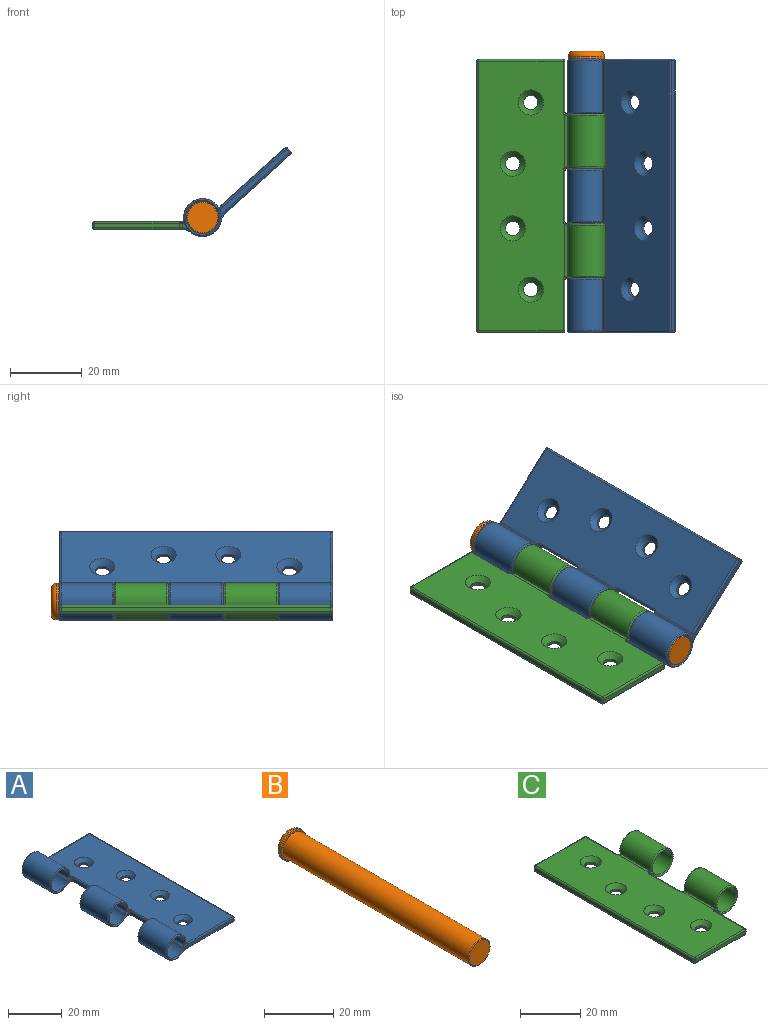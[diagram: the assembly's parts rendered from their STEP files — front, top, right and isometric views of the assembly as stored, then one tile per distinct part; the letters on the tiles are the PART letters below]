
ASSEMBLY  parts=3 mates=2
PART A: 94 faces, bbox 36.3x76x11.6 mm
  f0: cylinder r=5.25mm len=14.2mm, axis (0,1,0), area 412.4mm2, adj f2,f8,f69,f87
  f1: cylinder r=5.25mm len=14.2mm, axis (0,1,0), area 412.4mm2, adj f3,f9,f46,f78
  f2: plane 15.21x0.8mm, normal (0,0,-1), area 11.4mm2, adj f0,f4,f69,f71,f87,f90
  f3: plane 15.21x0.8mm, normal (0,0,-1), area 11.4mm2, adj f1,f5,f45,f46,f78,f80
  f4: cylinder r=4.5mm len=14.2mm, axis (0,1,0), area 382.9mm2, adj f2,f6,f71,f90
  f5: cylinder r=4.5mm len=14.2mm, axis (0,1,0), area 382.9mm2, adj f3,f7,f45,f80
  f6: cylinder r=2.39mm len=14.47mm, axis (0,1,0), area 36mm2, adj f4,f14,f73,f75,f92,f93
  f7: cylinder r=2.39mm len=14.33mm, axis (0,1,0), area 35.9mm2, adj f5,f14,f43,f82,f84
  f8: cylinder r=4.96mm len=14.47mm, axis (0,1,0), area 44.3mm2, adj f0,f16,f66,f68,f85,f88
  f9: cylinder r=4.96mm len=14.33mm, axis (0,1,0), area 44.3mm2, adj f1,f16,f48,f76,f77
  f10: cylinder r=5.25mm len=14.2mm, axis (0,1,0), area 412.4mm2, adj f11,f17,f51,f60
  f11: plane 15.21x0.8mm, normal (0,0,-1), area 11.4mm2, adj f10,f12,f51,f52,f60,f63
  f12: cylinder r=4.5mm len=14.2mm, axis (0,1,0), area 382.9mm2, adj f11,f13,f52,f63
  f13: cylinder r=2.39mm len=14.33mm, axis (0,1,0), area 35.9mm2, adj f12,f14,f49,f65,f67
  f14: plane 75x24mm, normal (0,0,1), area 1630.6mm2, adj f6,f7,f13,f21,f23,f25,f27,f41
  f15: plane 75x1.3mm, normal (1,0,0), area 97.5mm2, adj f38,f39,f42,f55
  f16: plane 75x24mm, normal (0,0,-1), area 1734.3mm2, adj f8,f9,f17,f20,f22,f24,f26,f50
  f17: cylinder r=4.96mm len=14.33mm, axis (0,1,0), area 44.3mm2, adj f10,f16,f54,f58,f61
  f18: plane 26.22x1.77mm, normal (0,-1,0), area 33.2mm2, adj f39,f47,f49,f52,f54,f56
  f19: plane 26.22x1.77mm, normal (0,1,0), area 33.2mm2, adj f38,f41,f43,f45,f48,f50
  f20: cylinder r=2mm len=4mm, axis (0,0,1), area 10.1mm2, adj f16,f21
  f21: cone r=2mm half-angle=45deg, axis (0,0,1), area 36.7mm2, adj f14,f20
  f22: cylinder r=2mm len=4mm, axis (0,0,1), area 10.1mm2, adj f16,f23
  f23: cone r=2mm half-angle=45deg, axis (0,0,1), area 36.7mm2, adj f14,f22
  f24: cylinder r=2mm len=4mm, axis (0,0,1), area 10.1mm2, adj f16,f25
  f25: cone r=2mm half-angle=45deg, axis (0,0,1), area 36.7mm2, adj f14,f24
  f26: cylinder r=2mm len=4mm, axis (0,0,1), area 10.1mm2, adj f16,f27
  f27: cone r=2mm half-angle=45deg, axis (0,0,1), area 36.7mm2, adj f14,f26
  f28: plane 14.2x1.3mm, normal (-1,0,0), area 18.5mm2, adj f34,f35,f81,f89
  f29: plane 1.72x1.7mm, normal (0,-1,0), area 1.3mm2, adj f34,f77,f80,f82
  f30: plane 1.72x1.7mm, normal (0,1,0), area 1.3mm2, adj f35,f88,f90,f92
  f31: plane 14.2x1.3mm, normal (-1,0,0), area 18.5mm2, adj f36,f37,f62,f72
  f32: plane 1.72x1.7mm, normal (0,1,0), area 1.3mm2, adj f36,f61,f63,f65
  f33: plane 1.72x1.7mm, normal (0,-1,0), area 1.3mm2, adj f37,f68,f71,f73
  f34: cylinder r=0.5mm len=1.32mm, axis (0,0,-1), area 1mm2, adj f28,f29,f76,f79,f84,f86
  f35: cylinder r=0.5mm len=1.32mm, axis (0,0,1), area 1mm2, adj f28,f30,f83,f85,f91,f93
  f36: cylinder r=0.5mm len=1.32mm, axis (0,0,-1), area 1mm2, adj f31,f32,f58,f59,f67,f70
  f37: cylinder r=0.5mm len=1.32mm, axis (0,0,1), area 1mm2, adj f31,f33,f64,f66,f74,f75
  f38: cylinder r=0.5mm len=1.3mm, axis (0,0,-1), area 1mm2, adj f15,f19,f40,f53
  f39: cylinder r=0.5mm len=1.3mm, axis (0,0,1), area 1mm2, adj f15,f18,f44,f57
  f40: sphere r=0.5mm, area 0.4mm2, adj f38,f41,f42
  f41: cylinder r=0.5mm len=24mm, axis (1,0,0), area 18.8mm2, adj f14,f19,f40,f43
  f42: cylinder r=0.5mm len=75mm, axis (0,1,0), area 58.9mm2, adj f14,f15,f40,f44
  f43: torus R=1.89mm, axis (0,-1,0), area 1.8mm2, adj f7,f19,f41,f45
  f44: sphere r=0.5mm, area 0.4mm2, adj f39,f42,f47
  f45: torus R=5mm, axis (0,-1,0), area 18.5mm2, adj f3,f5,f19,f43,f46,f48
  f46: torus R=4.75mm, axis (0,-1,0), area 18.7mm2, adj f1,f3,f45,f48
  f47: cylinder r=0.5mm len=24mm, axis (-1,0,0), area 18.8mm2, adj f14,f18,f44,f49
  f48: torus R=5.46mm, axis (0,-1,0), area 2.5mm2, adj f9,f19,f45,f46,f50
  f49: torus R=1.89mm, axis (0,-1,0), area 1.8mm2, adj f13,f18,f47,f52
  f50: cylinder r=0.5mm len=24mm, axis (-1,0,0), area 18.8mm2, adj f16,f19,f48,f53
  f51: torus R=4.75mm, axis (0,-1,0), area 18.7mm2, adj f10,f11,f52,f54
  f52: torus R=5mm, axis (0,-1,0), area 18.5mm2, adj f11,f12,f18,f49,f51,f54
  f53: sphere r=0.5mm, area 0.4mm2, adj f38,f50,f55
  f54: torus R=5.46mm, axis (0,-1,0), area 2.5mm2, adj f17,f18,f51,f52,f56
  f55: cylinder r=0.5mm len=75mm, axis (0,1,0), area 58.9mm2, adj f15,f16,f53,f57
  f56: cylinder r=0.5mm len=24mm, axis (1,0,0), area 18.8mm2, adj f16,f18,f54,f57
  f57: sphere r=0.5mm, area 0.4mm2, adj f39,f55,f56
  f58: bspline ~0.72x0.61mm, area 0.3mm2, adj f17,f36,f59,f61
  f59: torus R=1mm, axis (0,0,1), area 0.6mm2, adj f16,f36,f58,f62
  f60: torus R=4.75mm, axis (0,-1,0), area 18.7mm2, adj f10,f11,f61,f63
  f61: torus R=5.46mm, axis (0,-1,0), area 2.1mm2, adj f17,f32,f58,f60,f63
  f62: cylinder r=0.5mm len=14.2mm, axis (0,-1,0), area 11.2mm2, adj f16,f31,f59,f64
  f63: torus R=5mm, axis (0,-1,0), area 18.5mm2, adj f11,f12,f32,f60,f61,f65
  f64: torus R=1mm, axis (0,0,1), area 0.6mm2, adj f16,f37,f62,f66
  f65: torus R=1.89mm, axis (0,-1,0), area 1.4mm2, adj f13,f32,f63,f67
  f66: bspline ~0.72x0.61mm, area 0.3mm2, adj f8,f37,f64,f68
  f67: bspline ~0.83x0.6mm, area 0.3mm2, adj f13,f36,f65,f70
  f68: torus R=5.46mm, axis (0,-1,0), area 2.1mm2, adj f8,f33,f66,f69,f71
  f69: torus R=4.75mm, axis (0,-1,0), area 18.7mm2, adj f0,f2,f68,f71
  f70: torus R=1mm, axis (0,0,-1), area 0.6mm2, adj f14,f36,f67,f72
  f71: torus R=5mm, axis (0,-1,0), area 18.5mm2, adj f2,f4,f33,f68,f69,f73
  f72: cylinder r=0.5mm len=14.2mm, axis (0,-1,0), area 11.2mm2, adj f14,f31,f70,f74
  f73: torus R=1.89mm, axis (0,-1,0), area 1.4mm2, adj f6,f33,f71,f75
  f74: torus R=1mm, axis (0,0,-1), area 0.6mm2, adj f14,f37,f72,f75
  f75: bspline ~0.83x0.6mm, area 0.3mm2, adj f6,f37,f73,f74
  f76: bspline ~0.72x0.61mm, area 0.3mm2, adj f9,f34,f77,f79
  f77: torus R=5.46mm, axis (0,-1,0), area 2.1mm2, adj f9,f29,f76,f78,f80
  f78: torus R=4.75mm, axis (0,-1,0), area 18.7mm2, adj f1,f3,f77,f80
  f79: torus R=1mm, axis (0,0,1), area 0.6mm2, adj f16,f34,f76,f81
  f80: torus R=5mm, axis (0,-1,0), area 18.5mm2, adj f3,f5,f29,f77,f78,f82
  f81: cylinder r=0.5mm len=14.2mm, axis (0,1,0), area 11.2mm2, adj f16,f28,f79,f83
  f82: torus R=1.89mm, axis (0,-1,0), area 1.4mm2, adj f7,f29,f80,f84
  f83: torus R=1mm, axis (0,0,1), area 0.6mm2, adj f16,f35,f81,f85
  f84: bspline ~0.83x0.6mm, area 0.3mm2, adj f7,f34,f82,f86
  f85: bspline ~0.72x0.61mm, area 0.3mm2, adj f8,f35,f83,f88
  f86: torus R=1mm, axis (0,0,-1), area 0.6mm2, adj f14,f34,f84,f89
  f87: torus R=4.75mm, axis (0,-1,0), area 18.7mm2, adj f0,f2,f88,f90
  f88: torus R=5.46mm, axis (0,-1,0), area 2.1mm2, adj f8,f30,f85,f87,f90
  f89: cylinder r=0.5mm len=14.2mm, axis (0,-1,0), area 11.2mm2, adj f14,f28,f86,f91
  f90: torus R=5mm, axis (0,-1,0), area 18.5mm2, adj f2,f4,f30,f87,f88,f92
  f91: torus R=1mm, axis (0,0,-1), area 0.6mm2, adj f14,f35,f89,f93
  f92: torus R=1.89mm, axis (0,-1,0), area 1.4mm2, adj f6,f30,f90,f93
  f93: bspline ~0.83x0.6mm, area 0.3mm2, adj f6,f35,f91,f92
PART B: 8 faces, bbox 11x78.2x11 mm
  f0: cylinder r=4.4mm len=75.8mm, axis (0,1,0), area 2095.6mm2, adj f2,f5
  f1: plane 8.4x8.4mm, normal (0,-1,0), area 55.4mm2, adj f2
  f2: torus R=4.2mm, axis (0,-1,0), area 8.5mm2, adj f0,f1
  f3: cylinder r=5.1mm len=10.21mm, axis (0,-1,0), area 16mm2, adj f6,f7
  f4: plane 7.21x7.21mm, normal (0,1,0), area 40.8mm2, adj f6
  f5: plane 9.81x9.81mm, normal (0,-1,0), area 14.7mm2, adj f0,f7
  f6: torus R=3.6mm, axis (0,1,0), area 67.5mm2, adj f3,f4
  f7: torus R=4.9mm, axis (0,1,0), area 9.9mm2, adj f3,f5
PART C: 90 faces, bbox 36.3x76x11.6 mm
  f0: cylinder r=5.25mm len=14.2mm, axis (0,1,0), area 412.4mm2, adj f2,f8,f59,f83
  f1: cylinder r=5.25mm len=14.2mm, axis (0,1,0), area 412.4mm2, adj f3,f9,f46,f74
  f2: plane 15.21x0.8mm, normal (0,0,-1), area 11.4mm2, adj f0,f4,f59,f61,f83,f86
  f3: plane 15.21x0.8mm, normal (0,0,-1), area 11.4mm2, adj f1,f5,f46,f49,f74,f76
  f4: cylinder r=4.5mm len=14.2mm, axis (0,1,0), area 382.9mm2, adj f2,f6,f61,f86
  f5: cylinder r=4.5mm len=14.2mm, axis (0,1,0), area 382.9mm2, adj f3,f7,f49,f76
  f6: cylinder r=2.39mm len=14.47mm, axis (0,1,0), area 36mm2, adj f4,f10,f63,f65,f88,f89
  f7: cylinder r=2.39mm len=14.47mm, axis (0,1,0), area 36mm2, adj f5,f10,f51,f53,f78,f80
  f8: cylinder r=4.96mm len=14.47mm, axis (0,1,0), area 44.3mm2, adj f0,f12,f56,f58,f81,f84
  f9: cylinder r=4.96mm len=14.47mm, axis (0,1,0), area 44.3mm2, adj f1,f12,f44,f47,f72,f73
  f10: plane 75x24mm, normal (0,0,1), area 1623.5mm2, adj f6,f7,f16,f18,f20,f22,f55,f57
  f11: plane 75x1.3mm, normal (-1,0,0), area 97.5mm2, adj f36,f37,f43,f66
  f12: plane 75x24mm, normal (0,0,-1), area 1727.2mm2, adj f8,f9,f15,f17,f19,f21,f39,f40
  f13: plane 23.5x1.3mm, normal (0,-1,0), area 30.6mm2, adj f30,f37,f39,f62
  f14: plane 23.5x1.3mm, normal (0,1,0), area 30.6mm2, adj f34,f36,f48,f70
  f15: cylinder r=2mm len=4mm, axis (0,0,1), area 10.1mm2, adj f12,f16
  f16: cone r=2mm half-angle=45deg, axis (0,0,1), area 36.7mm2, adj f10,f15
  f17: cylinder r=2mm len=4mm, axis (0,0,1), area 10.1mm2, adj f12,f18
  f18: cone r=2mm half-angle=45deg, axis (0,0,1), area 36.7mm2, adj f10,f17
  f19: cylinder r=2mm len=4mm, axis (0,0,1), area 10.1mm2, adj f12,f20
  f20: cone r=2mm half-angle=45deg, axis (0,0,1), area 36.7mm2, adj f10,f19
  f21: cylinder r=2mm len=4mm, axis (0,0,1), area 10.1mm2, adj f12,f22
  f22: cone r=2mm half-angle=45deg, axis (0,0,1), area 36.7mm2, adj f10,f21
  f23: plane 14.2x1.3mm, normal (1,0,0), area 18.5mm2, adj f30,f31,f40,f57
  f24: plane 1.72x1.7mm, normal (0,-1,0), area 1.3mm2, adj f31,f47,f49,f51
  f25: plane 14.2x1.3mm, normal (1,0,0), area 18.5mm2, adj f32,f33,f77,f85
  f26: plane 1.72x1.7mm, normal (0,1,0), area 1.3mm2, adj f32,f73,f76,f78
  f27: plane 1.72x1.7mm, normal (0,-1,0), area 1.3mm2, adj f33,f84,f86,f88
  f28: plane 14.2x1.3mm, normal (1,0,0), area 18.5mm2, adj f34,f35,f52,f69
  f29: plane 1.72x1.7mm, normal (0,1,0), area 1.3mm2, adj f35,f58,f61,f63
  f30: cylinder r=0.5mm len=1.3mm, axis (0,0,1), area 1mm2, adj f13,f23,f38,f60
  f31: cylinder r=0.5mm len=1.32mm, axis (0,0,1), area 1mm2, adj f23,f24,f42,f44,f53,f55
  f32: cylinder r=0.5mm len=1.32mm, axis (0,0,-1), area 1mm2, adj f25,f26,f72,f75,f80,f82
  f33: cylinder r=0.5mm len=1.32mm, axis (0,0,1), area 1mm2, adj f25,f27,f79,f81,f87,f89
  f34: cylinder r=0.5mm len=1.3mm, axis (0,0,-1), area 1mm2, adj f14,f28,f50,f71
  f35: cylinder r=0.5mm len=1.32mm, axis (0,0,-1), area 1mm2, adj f28,f29,f54,f56,f65,f67
  f36: cylinder r=0.5mm len=1.3mm, axis (0,0,-1), area 1mm2, adj f11,f14,f45,f68
  f37: cylinder r=0.5mm len=1.3mm, axis (0,0,1), area 1mm2, adj f11,f13,f41,f64
  f38: sphere r=0.5mm, area 0.4mm2, adj f30,f39,f40
  f39: cylinder r=0.5mm len=23.5mm, axis (-1,0,0), area 18.5mm2, adj f12,f13,f38,f41
  f40: cylinder r=0.5mm len=14.2mm, axis (0,1,0), area 11.2mm2, adj f12,f23,f38,f42
  f41: sphere r=0.5mm, area 0.4mm2, adj f37,f39,f43
  f42: torus R=1mm, axis (0,0,1), area 0.6mm2, adj f12,f31,f40,f44
  f43: cylinder r=0.5mm len=75mm, axis (0,1,0), area 58.9mm2, adj f11,f12,f41,f45
  f44: bspline ~0.72x0.61mm, area 0.3mm2, adj f9,f31,f42,f47
  f45: sphere r=0.5mm, area 0.4mm2, adj f36,f43,f48
  f46: torus R=4.75mm, axis (0,1,0), area 18.7mm2, adj f1,f3,f47,f49
  f47: torus R=5.46mm, axis (0,1,0), area 2.1mm2, adj f9,f24,f44,f46,f49
  f48: cylinder r=0.5mm len=23.5mm, axis (1,0,0), area 18.5mm2, adj f12,f14,f45,f50
  f49: torus R=5mm, axis (0,1,0), area 18.5mm2, adj f3,f5,f24,f46,f47,f51
  f50: sphere r=0.5mm, area 0.4mm2, adj f34,f48,f52
  f51: torus R=1.89mm, axis (0,1,0), area 1.4mm2, adj f7,f24,f49,f53
  f52: cylinder r=0.5mm len=14.2mm, axis (0,-1,0), area 11.2mm2, adj f12,f28,f50,f54
  f53: bspline ~0.83x0.6mm, area 0.3mm2, adj f7,f31,f51,f55
  f54: torus R=1mm, axis (0,0,1), area 0.6mm2, adj f12,f35,f52,f56
  f55: torus R=1mm, axis (0,0,-1), area 0.6mm2, adj f10,f31,f53,f57
  f56: bspline ~0.72x0.61mm, area 0.3mm2, adj f8,f35,f54,f58
  f57: cylinder r=0.5mm len=14.2mm, axis (0,1,0), area 11.2mm2, adj f10,f23,f55,f60
  f58: torus R=5.46mm, axis (0,1,0), area 2.1mm2, adj f8,f29,f56,f59,f61
  f59: torus R=4.75mm, axis (0,1,0), area 18.7mm2, adj f0,f2,f58,f61
  f60: sphere r=0.5mm, area 0.4mm2, adj f30,f57,f62
  f61: torus R=5mm, axis (0,1,0), area 18.5mm2, adj f2,f4,f29,f58,f59,f63
  f62: cylinder r=0.5mm len=23.5mm, axis (1,0,0), area 18.5mm2, adj f10,f13,f60,f64
  f63: torus R=1.89mm, axis (0,1,0), area 1.4mm2, adj f6,f29,f61,f65
  f64: sphere r=0.5mm, area 0.4mm2, adj f37,f62,f66
  f65: bspline ~0.83x0.6mm, area 0.3mm2, adj f6,f35,f63,f67
  f66: cylinder r=0.5mm len=75mm, axis (0,1,0), area 58.9mm2, adj f10,f11,f64,f68
  f67: torus R=1mm, axis (0,0,-1), area 0.6mm2, adj f10,f35,f65,f69
  f68: sphere r=0.5mm, area 0.4mm2, adj f36,f66,f70
  f69: cylinder r=0.5mm len=14.2mm, axis (0,1,0), area 11.2mm2, adj f10,f28,f67,f71
  f70: cylinder r=0.5mm len=23.5mm, axis (-1,0,0), area 18.5mm2, adj f10,f14,f68,f71
  f71: sphere r=0.5mm, area 0.4mm2, adj f34,f69,f70
  f72: bspline ~0.72x0.61mm, area 0.3mm2, adj f9,f32,f73,f75
  f73: torus R=5.46mm, axis (0,1,0), area 2.1mm2, adj f9,f26,f72,f74,f76
  f74: torus R=4.75mm, axis (0,1,0), area 18.7mm2, adj f1,f3,f73,f76
  f75: torus R=1mm, axis (0,0,1), area 0.6mm2, adj f12,f32,f72,f77
  f76: torus R=5mm, axis (0,1,0), area 18.5mm2, adj f3,f5,f26,f73,f74,f78
  f77: cylinder r=0.5mm len=14.2mm, axis (0,1,0), area 11.2mm2, adj f12,f25,f75,f79
  f78: torus R=1.89mm, axis (0,1,0), area 1.4mm2, adj f7,f26,f76,f80
  f79: torus R=1mm, axis (0,0,1), area 0.6mm2, adj f12,f33,f77,f81
  f80: bspline ~0.83x0.6mm, area 0.3mm2, adj f7,f32,f78,f82
  f81: bspline ~0.72x0.61mm, area 0.3mm2, adj f8,f33,f79,f84
  f82: torus R=1mm, axis (0,0,-1), area 0.6mm2, adj f10,f32,f80,f85
  f83: torus R=4.75mm, axis (0,1,0), area 18.7mm2, adj f0,f2,f84,f86
  f84: torus R=5.46mm, axis (0,1,0), area 2.1mm2, adj f8,f27,f81,f83,f86
  f85: cylinder r=0.5mm len=14.2mm, axis (0,1,0), area 11.2mm2, adj f10,f25,f82,f87
  f86: torus R=5mm, axis (0,1,0), area 18.5mm2, adj f2,f4,f27,f83,f84,f88
  f87: torus R=1mm, axis (0,0,-1), area 0.6mm2, adj f10,f33,f85,f89
  f88: torus R=1.89mm, axis (0,1,0), area 1.4mm2, adj f6,f27,f86,f89
  f89: bspline ~0.83x0.6mm, area 0.3mm2, adj f6,f33,f87,f88
PLACE A rot(axis=(0,-1,0),42.1deg) t=(35.16,-9.03,0.52)mm
PLACE B t=(32.94,-9.02,4.28)mm
PLACE C t=(32.94,-9.06,4.28)mm
MATE revolute C.f0 <-> A.f0  axis (0,1,0) through (38.94,-69.85,5.28)mm
MATE revolute B.f0 <-> A.f0  axis (0,-1,0) through (38.94,-85.02,5.28)mm
